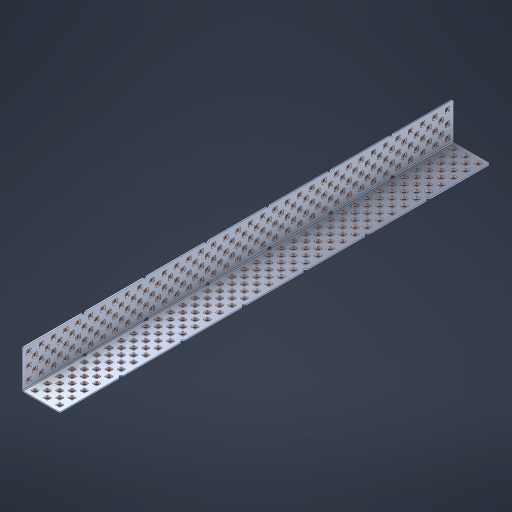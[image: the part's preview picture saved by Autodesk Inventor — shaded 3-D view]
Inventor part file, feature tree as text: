
AUTODESK INVENTOR PART (.ipt)
format: ipt  version: 2023 (Build 270158000, 158)  size: 3,399,680 bytes
history: native  units: in
note: dims shown in document units (in); Inventor stores cm internally (conversion verified against a paired STEP export)
features: other x352, extrude x344, sheet_metal_op x8, sketch x7, pattern_linear x3, mirror x1, chamfer x1
ambient origin geometry x8: Origin, YZ Plane, XZ Plane, XY Plane, X Axis, Y Axis, Z Axis, Center Point
bodies: Solid1 (feature_tree), Body (feature_tree)
feature tree (716):
  sheet_metal_op  "Flanges"
  sheet_metal_op  "Body Pattern"
  pattern_linear  "Center Double"  Spacing1=1.5in  [1 undecoded]
  pattern_linear  "Center Pattern"  Spacing1=0.1875in  [1 undecoded]
  other  "Arc Length"
  pattern_linear  "Notch Pattern"  Spacing1=0.0469in  [1 undecoded]
  other  "Diagonal Plane"
  mirror  "Everything Mirrored"
  chamfer  "End Chamfer"
  sketch  "Sketch1"  dims[d0=1.5in]
  other  "Plate1"
  sketch  "Sketch2"  dims[d1=17.5in]
  other  "Plate2"
  sheet_metal_op  "Bend1"
  sheet_metal_op  "Corner1"
  sketch  "Sketch8"  dims[d2=0.0469in]
  sketch  "Sketch9"  dims[d3=0.0469in]
  other  "Srf91"
  sheet_metal_op  "Body Pattern Sketch"
  other  "Srf92"
  sketch  "Sketch13"  dims[d4=0.0234in]
  sketch  "Sketch15"  dims[d5=0.0938in]
  sketch  "Sketch16"  dims[d6=0.0469in d7=1.5in d8=90.0deg d9=0.0312in d10=0.1875in d11=0.0469in d12=0.0469in d49=0.182in d50=0.02in d52=0.25in d53=0.0469in d54=0.0in d55=0.172in d56=1.0in d57=0.0in d85=0.1473in d86=0.1659in d89=0.0469in d90=0.0in d91=0.04in d92=0.0491in d95=2.5in d96=0.04in d97=0.25in d98=45.0deg d106=0.182in d107=0.02in d110=0.0469in d111=0.0in d112=0.172in d113=0.5in d114=0.0in d117=0.5in d126=0.0491in d127=0.1227in d128=0.08in d129=0.04in d130=2.5in d131=0.25in d132=13.7795in d134=0.5in d135=1.1811in d137=0.5in d140=0.5in d141=1.0in d142=0.3937in d144=0.5in d145=0.071in d146=0.7874in d148=0.5in]
  other  "Srf786"
  other  "Srf856"
  other  "Srf889"
  other  "Srf890"
  other  "Srf891"
  other  "Srf1275"
  other  "Srf1276"
  other  "Srf1278"
  other  "Srf1277"
  other  "Srf1285"
  other  "Srf1286"
  other  "Srf1287"
  other  "Srf1445"
  other  "Srf1446"
  other  "Srf1447"
  other  "Srf1448"
  other  "Srf1449"
  other  "Srf1537"
  other  "Srf1538"
  other  "Srf1539"
  other  "Srf1540"
  other  "Srf1541"
  other  "Srf1807"
  other  "Srf1808"
  other  "Srf1809"
  other  "Srf1810"
  other  "Srf1811"
  other  "Srf1812"
  other  "Srf1813"
  other  "Srf1814"
  other  "Srf1815"
  other  "Srf1816"
  other  "Srf1817"
  other  "Srf1818"
  other  "Srf1819"
  other  "Srf1820"
  other  "Srf1821"
  other  "Srf1822"
  other  "Srf1823"
  other  "Srf1824"
  other  "Srf1825"
  other  "Srf1826"
  other  "Srf1827"
  other  "Srf1828"
  other  "Srf1829"
  other  "Srf1830"
  other  "Srf1831"
  other  "Srf1959"
  other  "Srf1960"
  other  "Srf1961"
  other  "Srf1962"
  other  "Srf1963"
  other  "Srf1964"
  other  "Srf1965"
  other  "Srf1966"
  other  "Srf1967"
  other  "Srf1968"
  other  "Srf1969"
  other  "Srf1970"
  other  "Srf1971"
  other  "Srf1972"
  other  "Srf1973"
  other  "Srf1974"
  other  "Srf1975"
  other  "Srf1976"
  other  "Srf1977"
  other  "Srf1978"
  other  "Srf1979"
  other  "Srf1980"
  other  "Srf1981"
  other  "Srf1982"
  other  "Srf1983"
  other  "Srf2009"
  other  "Srf2010"
  other  "Srf2011"
  other  "Srf2012"
  other  "Srf2013"
  other  "Srf2014"
  other  "Srf2015"
  other  "Srf2016"
  other  "Srf2017"
  other  "Srf2018"
  other  "Srf2019"
  other  "Srf2020"
  other  "Srf2021"
  other  "Srf2022"
  other  "Srf2023"
  other  "Srf2024"
  other  "Srf2025"
  other  "Srf2026"
  other  "Srf2027"
  other  "Srf2028"
  other  "Srf2029"
  other  "Srf2030"
  other  "Srf2031"
  other  "Srf2032"
  other  "Srf2033"
  other  "Srf2034"
  other  "Srf2035"
  other  "Srf2036"
  other  "Srf2037"
  other  "Srf2038"
  other  "Srf2039"
  other  "Srf2040"
  other  "Srf2041"
  other  "Srf2042"
  other  "Srf2043"
  other  "Srf2044"
  other  "Srf2045"
  other  "Srf2046"
  other  "Srf2047"
  other  "Srf2048"
  other  "Srf2049"
  other  "Srf2050"
  other  "Srf2051"
  other  "Srf2052"
  other  "Srf2053"
  other  "Srf2054"
  other  "Srf2055"
  other  "Srf2056"
  other  "Srf2057"
  other  "Srf2058"
  other  "Srf2059"
  other  "Srf2060"
  other  "Srf2061"
  other  "Srf2062"
  other  "Srf2063"
  other  "Srf2064"
  other  "Srf2065"
  other  "Srf2066"
  other  "Srf2067"
  other  "Srf2068"
  other  "Srf2069"
  other  "Srf2070"
  other  "Srf2071"
  other  "Srf2072"
  other  "Srf2073"
  other  "Srf2074"
  other  "Srf2075"
  other  "Srf2076"
  other  "Srf2077"
  other  "Srf2078"
  other  "Srf2079"
  other  "Srf2080"
  other  "Srf2081"
  other  "Srf2082"
  other  "Srf2083"
  other  "Srf2084"
  other  "Srf2085"
  other  "Srf2086"
  other  "Srf2087"
  other  "Srf2088"
  other  "Srf2089"
  other  "Srf2090"
  other  "Srf2091"
  other  "Srf2092"
  other  "Srf2093"
  other  "Srf2094"
  other  "Srf2095"
  other  "Srf2096"
  other  "Srf2097"
  other  "Srf2098"
  other  "Srf2099"
  other  "Srf2100"
  other  "Srf2101"
  other  "Srf2102"
  other  "Srf2103"
  other  "Srf2104"
  other  "Srf2105"
  other  "Srf2106"
  other  "Srf2107"
  other  "Srf2108"
  other  "Srf2109"
  other  "Srf2110"
  other  "Srf2111"
  other  "Srf2112"
  other  "Srf2113"
  other  "Srf2114"
  other  "Srf2115"
  other  "Srf2116"
  other  "Srf2117"
  other  "Srf2118"
  other  "Srf2119"
  other  "Srf2120"
  other  "Srf2121"
  other  "Srf2122"
  other  "Srf2123"
  other  "Srf2124"
  other  "Srf2125"
  other  "Srf2126"
  other  "Srf2127"
  other  "Srf2128"
  other  "Srf2129"
  other  "Srf2130"
  other  "Srf2131"
  other  "Srf2132"
  other  "Srf2133"
  other  "Srf2134"
  other  "Srf2135"
  other  "Srf2136"
  other  "Srf2137"
  other  "Srf2138"
  other  "Srf2139"
  other  "Srf2140"
  other  "Srf2141"
  other  "Srf2142"
  other  "Srf2143"
  other  "Srf2144"
  other  "Srf2145"
  other  "Srf2146"
  other  "Srf2147"
  other  "Srf2148"
  other  "Srf2149"
  other  "Srf2150"
  other  "Srf2151"
  other  "Srf2152"
  other  "Srf2153"
  other  "Srf2154"
  other  "Srf2155"
  other  "Srf2156"
  other  "Srf2157"
  other  "Srf2158"
  other  "Srf2159"
  other  "Srf2160"
  other  "Srf2161"
  other  "Srf2162"
  other  "Srf2163"
  other  "Srf2164"
  other  "Srf2165"
  other  "Srf2166"
  other  "Srf2167"
  other  "Srf2168"
  other  "Srf2169"
  other  "Srf2170"
  other  "Srf2171"
  other  "Srf2172"
  other  "Srf2173"
  other  "Srf2174"
  other  "Srf2175"
  other  "Srf2176"
  other  "Srf2177"
  other  "Srf2178"
  other  "Srf2179"
  other  "Srf2180"
  other  "Srf2181"
  other  "Srf2182"
  other  "Srf2183"
  other  "Srf2184"
  other  "Srf2185"
  other  "Srf2186"
  other  "Srf2187"
  other  "Srf2188"
  other  "Srf2189"
  other  "Srf2190"
  other  "Srf2191"
  other  "Srf2192"
  other  "Srf2193"
  other  "Srf2194"
  other  "Srf2195"
  other  "Srf2196"
  other  "Srf2197"
  other  "Srf2198"
  other  "Srf2199"
  other  "Srf2200"
  other  "Srf2201"
  other  "Srf2202"
  other  "Srf2203"
  other  "Srf2204"
  other  "Srf2205"
  other  "Srf2206"
  other  "Srf2207"
  other  "Srf2208"
  other  "Srf2209"
  other  "Srf2210"
  other  "Srf2211"
  other  "Srf2212"
  other  "Srf2213"
  other  "Srf2214"
  other  "Srf2215"
  other  "Srf2216"
  other  "Srf2217"
  other  "Srf2218"
  other  "Srf2219"
  other  "Srf2220"
  other  "Srf2221"
  other  "Srf2222"
  other  "Srf2223"
  other  "Srf2224"
  other  "Srf2225"
  other  "Srf2226"
  other  "Srf2227"
  other  "Srf2228"
  other  "Srf2229"
  other  "Srf2230"
  other  "Srf2231"
  other  "Srf2232"
  other  "Srf2233"
  other  "Srf2234"
  other  "Srf2235"
  other  "Srf2236"
  other  "Srf2237"
  other  "Srf2238"
  other  "Srf2239"
  other  "Srf2240"
  other  "Srf2241"
  other  "Srf2242"
  other  "Srf2243"
  other  "Srf2244"
  other  "Srf2245"
  other  "Srf2246"
  other  "Srf2247"
  other  "Srf2248"
  other  "Srf2249"
  other  "Srf2250"
  other  "Srf2251"
  other  "Srf2252"
  other  "Srf2253"
  other  "Srf2254"
  other  "Srf2255"
  other  "Srf2256"
  other  "Srf2257"
  other  "Srf2258"
  other  "Srf2259"
  other  "Srf2260"
  other  "Srf2261"
  other  "Srf2262"
  other  "Srf2263"
  other  "Srf2264"
  other  "Srf2265"
  other  "Srf2266"
  other  "Srf2267"
  other  "Srf2268"
  other  "Srf2269"
  other  "Srf2270"
  other  "Srf2271"
  other  "Srf2272"
  other  "Srf2273"
  other  "Srf2274"
  other  "Srf2275"
  other  "Srf2276"
  other  "Srf2277"
  other  "Srf2278"
  other  "Srf2279"
  other  "Srf2280"
  sheet_metal_op  "Body Stamp"
  sheet_metal_op  "Body Circle"
  other  "Center Stamp"
  other  "Center Circle"
  sheet_metal_op  "Notch"
  extrude  "ExtrusionSrf92"  Depth=0.0469in
  extrude  "ExtrusionSrf856"  Depth=0.3937in
  extrude  "ExtrusionSrf889"  Depth=0.02in
  extrude  "ExtrusionSrf890"  Depth=0.25in
  extrude  "ExtrusionSrf891"  Depth=0.0469in
  extrude  "ExtrusionSrf1275"  TaperAngle=0.0deg  [1 undecoded]
  extrude  "ExtrusionSrf1276"  Depth=0.3937in
  extrude  "ExtrusionSrf1277"  Depth=0.3937in TaperAngle=0.0deg
  extrude  "ExtrusionSrf1345"  Depth=0.3937in
  extrude  "ExtrusionSrf1346"  Depth=0.3937in
  extrude  "ExtrusionSrf1347"  Depth=0.0469in
  extrude  "ExtrusionSrf1348"  Depth=0.3937in TaperAngle=0.0deg
  extrude  "ExtrusionSrf1445"  Depth=0.3937in
  extrude  "ExtrusionSrf1446"  Depth=0.25in TaperAngle=45.0deg
  extrude  "ExtrusionSrf1447"  Depth=0.3937in
  extrude  "ExtrusionSrf1448"  Depth=0.02in
  extrude  "ExtrusionSrf1449"  Depth=0.0469in
  extrude  "ExtrusionSrf1537"  TaperAngle=0.0deg  [1 undecoded]
  extrude  "ExtrusionSrf1538"  Depth=0.3937in
  extrude  "ExtrusionSrf1539"  Depth=0.3937in TaperAngle=0.0deg
  extrude  "ExtrusionSrf1540"  Depth=0.3937in
  extrude  "ExtrusionSrf1541"  Depth=0.3937in
  extrude  "ExtrusionSrf1807"  Depth=0.3937in
  extrude  "ExtrusionSrf1808"  Depth=0.3937in
  extrude  "ExtrusionSrf1809"  Depth=0.3937in
  extrude  "ExtrusionSrf1810"  Depth=0.3937in
  extrude  "ExtrusionSrf1811"  Depth=0.25in
  extrude  "ExtrusionSrf1812"  Depth=0.3937in
  extrude  "ExtrusionSrf1813"  Depth=0.3937in
  extrude  "ExtrusionSrf1814"  Depth=0.3937in
  extrude  "ExtrusionSrf1815"  Depth=0.3937in
  extrude  "ExtrusionSrf1816"  Depth=0.3937in
  extrude  "ExtrusionSrf1817"  Depth=0.3937in
  extrude  "ExtrusionSrf1818"  Depth=0.3937in
  extrude  "ExtrusionSrf1819"  [1 undecoded]
  extrude  "ExtrusionSrf1820"  [1 undecoded]
  extrude  "ExtrusionSrf1821"  [1 undecoded]
  extrude  "ExtrusionSrf1822"  [1 undecoded]
  extrude  "ExtrusionSrf1823"  [1 undecoded]
  extrude  "ExtrusionSrf1824"  [1 undecoded]
  extrude  "ExtrusionSrf1825"  [1 undecoded]
  extrude  "ExtrusionSrf1826"  [1 undecoded]
  extrude  "ExtrusionSrf1827"  [1 undecoded]
  extrude  "ExtrusionSrf1828"  [1 undecoded]
  extrude  "ExtrusionSrf1829"  [1 undecoded]
  extrude  "ExtrusionSrf1830"  [1 undecoded]
  extrude  "ExtrusionSrf1831"  [1 undecoded]
  extrude  "ExtrusionSrf1959"  [1 undecoded]
  extrude  "ExtrusionSrf1960"  [1 undecoded]
  extrude  "ExtrusionSrf1961"  [1 undecoded]
  extrude  "ExtrusionSrf1962"  [1 undecoded]
  extrude  "ExtrusionSrf1963"  [1 undecoded]
  extrude  "ExtrusionSrf1964"  [1 undecoded]
  extrude  "ExtrusionSrf1965"  [1 undecoded]
  extrude  "ExtrusionSrf1966"  [1 undecoded]
  extrude  "ExtrusionSrf1967"  [1 undecoded]
  extrude  "ExtrusionSrf1968"  [1 undecoded]
  extrude  "ExtrusionSrf1969"  [1 undecoded]
  extrude  "ExtrusionSrf1970"  [1 undecoded]
  extrude  "ExtrusionSrf1971"  [1 undecoded]
  extrude  "ExtrusionSrf1972"  [1 undecoded]
  extrude  "ExtrusionSrf1973"  [1 undecoded]
  extrude  "ExtrusionSrf1974"  [1 undecoded]
  extrude  "ExtrusionSrf1975"  [1 undecoded]
  extrude  "ExtrusionSrf1976"  [1 undecoded]
  extrude  "ExtrusionSrf1977"  [1 undecoded]
  extrude  "ExtrusionSrf1978"  [1 undecoded]
  extrude  "ExtrusionSrf1979"  [1 undecoded]
  extrude  "ExtrusionSrf1980"  [1 undecoded]
  extrude  "ExtrusionSrf1981"  [1 undecoded]
  extrude  "ExtrusionSrf1982"  [1 undecoded]
  extrude  "ExtrusionSrf1983"  [1 undecoded]
  extrude  "ExtrusionSrf2009"  [1 undecoded]
  extrude  "ExtrusionSrf2010"  [1 undecoded]
  extrude  "ExtrusionSrf2011"  [1 undecoded]
  extrude  "ExtrusionSrf2012"  [1 undecoded]
  extrude  "ExtrusionSrf2013"  [1 undecoded]
  extrude  "ExtrusionSrf2014"  [1 undecoded]
  extrude  "ExtrusionSrf2015"  [1 undecoded]
  extrude  "ExtrusionSrf2016"  [1 undecoded]
  extrude  "ExtrusionSrf2017"  [1 undecoded]
  extrude  "ExtrusionSrf2018"  [1 undecoded]
  extrude  "ExtrusionSrf2019"  [1 undecoded]
  extrude  "ExtrusionSrf2020"  [1 undecoded]
  extrude  "ExtrusionSrf2021"  [1 undecoded]
  extrude  "ExtrusionSrf2022"  [1 undecoded]
  extrude  "ExtrusionSrf2023"  [1 undecoded]
  extrude  "ExtrusionSrf2024"  [1 undecoded]
  extrude  "ExtrusionSrf2025"  [1 undecoded]
  extrude  "ExtrusionSrf2026"  [1 undecoded]
  extrude  "ExtrusionSrf2027"  [1 undecoded]
  extrude  "ExtrusionSrf2028"  [1 undecoded]
  extrude  "ExtrusionSrf2029"  [1 undecoded]
  extrude  "ExtrusionSrf2030"  [1 undecoded]
  extrude  "ExtrusionSrf2031"  [1 undecoded]
  extrude  "ExtrusionSrf2032"  [1 undecoded]
  extrude  "ExtrusionSrf2033"  [1 undecoded]
  extrude  "ExtrusionSrf2034"  [1 undecoded]
  extrude  "ExtrusionSrf2035"  [1 undecoded]
  extrude  "ExtrusionSrf2036"  [1 undecoded]
  extrude  "ExtrusionSrf2037"  [1 undecoded]
  extrude  "ExtrusionSrf2038"  [1 undecoded]
  extrude  "ExtrusionSrf2039"  [1 undecoded]
  extrude  "ExtrusionSrf2040"  [1 undecoded]
  extrude  "ExtrusionSrf2041"  [1 undecoded]
  extrude  "ExtrusionSrf2042"  [1 undecoded]
  extrude  "ExtrusionSrf2043"  [1 undecoded]
  extrude  "ExtrusionSrf2044"  [1 undecoded]
  extrude  "ExtrusionSrf2045"  [1 undecoded]
  extrude  "ExtrusionSrf2046"  [1 undecoded]
  extrude  "ExtrusionSrf2047"  [1 undecoded]
  extrude  "ExtrusionSrf2048"  [1 undecoded]
  extrude  "ExtrusionSrf2049"  [1 undecoded]
  extrude  "ExtrusionSrf2050"  [1 undecoded]
  extrude  "ExtrusionSrf2051"  [1 undecoded]
  extrude  "ExtrusionSrf2052"  [1 undecoded]
  extrude  "ExtrusionSrf2053"  [1 undecoded]
  extrude  "ExtrusionSrf2054"  [1 undecoded]
  extrude  "ExtrusionSrf2055"  [1 undecoded]
  extrude  "ExtrusionSrf2056"  [1 undecoded]
  extrude  "ExtrusionSrf2057"  [1 undecoded]
  extrude  "ExtrusionSrf2058"  [1 undecoded]
  extrude  "ExtrusionSrf2059"  [1 undecoded]
  extrude  "ExtrusionSrf2060"  [1 undecoded]
  extrude  "ExtrusionSrf2061"  [1 undecoded]
  extrude  "ExtrusionSrf2062"  [1 undecoded]
  extrude  "ExtrusionSrf2063"  [1 undecoded]
  extrude  "ExtrusionSrf2064"  [1 undecoded]
  extrude  "ExtrusionSrf2065"  [1 undecoded]
  extrude  "ExtrusionSrf2066"  [1 undecoded]
  extrude  "ExtrusionSrf2067"  [1 undecoded]
  extrude  "ExtrusionSrf2068"  [1 undecoded]
  extrude  "ExtrusionSrf2069"  [1 undecoded]
  extrude  "ExtrusionSrf2070"  [1 undecoded]
  extrude  "ExtrusionSrf2071"  [1 undecoded]
  extrude  "ExtrusionSrf2072"  [1 undecoded]
  extrude  "ExtrusionSrf2073"  [1 undecoded]
  extrude  "ExtrusionSrf2074"  [1 undecoded]
  extrude  "ExtrusionSrf2075"  [1 undecoded]
  extrude  "ExtrusionSrf2076"  [1 undecoded]
  extrude  "ExtrusionSrf2077"  [1 undecoded]
  extrude  "ExtrusionSrf2078"  [1 undecoded]
  extrude  "ExtrusionSrf2079"  [1 undecoded]
  extrude  "ExtrusionSrf2080"  [1 undecoded]
  extrude  "ExtrusionSrf2081"  [1 undecoded]
  extrude  "ExtrusionSrf2082"  [1 undecoded]
  extrude  "ExtrusionSrf2083"  [1 undecoded]
  extrude  "ExtrusionSrf2084"  [1 undecoded]
  extrude  "ExtrusionSrf2085"  [1 undecoded]
  extrude  "ExtrusionSrf2086"  [1 undecoded]
  extrude  "ExtrusionSrf2087"  [1 undecoded]
  extrude  "ExtrusionSrf2088"  [1 undecoded]
  extrude  "ExtrusionSrf2089"  [1 undecoded]
  extrude  "ExtrusionSrf2090"  [1 undecoded]
  extrude  "ExtrusionSrf2091"  [1 undecoded]
  extrude  "ExtrusionSrf2092"  [1 undecoded]
  extrude  "ExtrusionSrf2093"  [1 undecoded]
  extrude  "ExtrusionSrf2094"  [1 undecoded]
  extrude  "ExtrusionSrf2095"  [1 undecoded]
  extrude  "ExtrusionSrf2096"  [1 undecoded]
  extrude  "ExtrusionSrf2097"  [1 undecoded]
  extrude  "ExtrusionSrf2098"  [1 undecoded]
  extrude  "ExtrusionSrf2099"  [1 undecoded]
  extrude  "ExtrusionSrf2100"  [1 undecoded]
  extrude  "ExtrusionSrf2101"  [1 undecoded]
  extrude  "ExtrusionSrf2102"  [1 undecoded]
  extrude  "ExtrusionSrf2103"  [1 undecoded]
  extrude  "ExtrusionSrf2104"  [1 undecoded]
  extrude  "ExtrusionSrf2105"  [1 undecoded]
  extrude  "ExtrusionSrf2106"  [1 undecoded]
  extrude  "ExtrusionSrf2107"  [1 undecoded]
  extrude  "ExtrusionSrf2108"  [1 undecoded]
  extrude  "ExtrusionSrf2109"  [1 undecoded]
  extrude  "ExtrusionSrf2110"  [1 undecoded]
  extrude  "ExtrusionSrf2111"  [1 undecoded]
  extrude  "ExtrusionSrf2112"  [1 undecoded]
  extrude  "ExtrusionSrf2113"  [1 undecoded]
  extrude  "ExtrusionSrf2114"  [1 undecoded]
  extrude  "ExtrusionSrf2115"  [1 undecoded]
  extrude  "ExtrusionSrf2116"  [1 undecoded]
  extrude  "ExtrusionSrf2117"  [1 undecoded]
  extrude  "ExtrusionSrf2118"  [1 undecoded]
  extrude  "ExtrusionSrf2119"  [1 undecoded]
  extrude  "ExtrusionSrf2120"  [1 undecoded]
  extrude  "ExtrusionSrf2121"  [1 undecoded]
  extrude  "ExtrusionSrf2122"  [1 undecoded]
  extrude  "ExtrusionSrf2123"  [1 undecoded]
  extrude  "ExtrusionSrf2124"  [1 undecoded]
  extrude  "ExtrusionSrf2125"  [1 undecoded]
  extrude  "ExtrusionSrf2126"  [1 undecoded]
  extrude  "ExtrusionSrf2127"  [1 undecoded]
  extrude  "ExtrusionSrf2128"  [1 undecoded]
  extrude  "ExtrusionSrf2129"  [1 undecoded]
  extrude  "ExtrusionSrf2130"  [1 undecoded]
  extrude  "ExtrusionSrf2131"  [1 undecoded]
  extrude  "ExtrusionSrf2132"  [1 undecoded]
  extrude  "ExtrusionSrf2133"  [1 undecoded]
  extrude  "ExtrusionSrf2134"  [1 undecoded]
  extrude  "ExtrusionSrf2135"  [1 undecoded]
  extrude  "ExtrusionSrf2136"  [1 undecoded]
  extrude  "ExtrusionSrf2137"  [1 undecoded]
  extrude  "ExtrusionSrf2138"  [1 undecoded]
  extrude  "ExtrusionSrf2139"  [1 undecoded]
  extrude  "ExtrusionSrf2140"  [1 undecoded]
  extrude  "ExtrusionSrf2141"  [1 undecoded]
  extrude  "ExtrusionSrf2142"  [1 undecoded]
  extrude  "ExtrusionSrf2143"  [1 undecoded]
  extrude  "ExtrusionSrf2144"  [1 undecoded]
  extrude  "ExtrusionSrf2145"  [1 undecoded]
  extrude  "ExtrusionSrf2146"  [1 undecoded]
  extrude  "ExtrusionSrf2147"  [1 undecoded]
  extrude  "ExtrusionSrf2148"  [1 undecoded]
  extrude  "ExtrusionSrf2149"  [1 undecoded]
  extrude  "ExtrusionSrf2150"  [1 undecoded]
  extrude  "ExtrusionSrf2151"  [1 undecoded]
  extrude  "ExtrusionSrf2152"  [1 undecoded]
  extrude  "ExtrusionSrf2153"  [1 undecoded]
  extrude  "ExtrusionSrf2154"  [1 undecoded]
  extrude  "ExtrusionSrf2155"  [1 undecoded]
  extrude  "ExtrusionSrf2156"  [1 undecoded]
  extrude  "ExtrusionSrf2157"  [1 undecoded]
  extrude  "ExtrusionSrf2158"  [1 undecoded]
  extrude  "ExtrusionSrf2159"  [1 undecoded]
  extrude  "ExtrusionSrf2160"  [1 undecoded]
  extrude  "ExtrusionSrf2161"  [1 undecoded]
  extrude  "ExtrusionSrf2162"  [1 undecoded]
  extrude  "ExtrusionSrf2163"  [1 undecoded]
  extrude  "ExtrusionSrf2164"  [1 undecoded]
  extrude  "ExtrusionSrf2165"  [1 undecoded]
  extrude  "ExtrusionSrf2166"  [1 undecoded]
  extrude  "ExtrusionSrf2167"  [1 undecoded]
  extrude  "ExtrusionSrf2168"  [1 undecoded]
  extrude  "ExtrusionSrf2169"  [1 undecoded]
  extrude  "ExtrusionSrf2170"  [1 undecoded]
  extrude  "ExtrusionSrf2171"  [1 undecoded]
  extrude  "ExtrusionSrf2172"  [1 undecoded]
  extrude  "ExtrusionSrf2173"  [1 undecoded]
  extrude  "ExtrusionSrf2174"  [1 undecoded]
  extrude  "ExtrusionSrf2175"  [1 undecoded]
  extrude  "ExtrusionSrf2176"  [1 undecoded]
  extrude  "ExtrusionSrf2177"  [1 undecoded]
  extrude  "ExtrusionSrf2178"  [1 undecoded]
  extrude  "ExtrusionSrf2179"  [1 undecoded]
  extrude  "ExtrusionSrf2180"  [1 undecoded]
  extrude  "ExtrusionSrf2181"  [1 undecoded]
  extrude  "ExtrusionSrf2182"  [1 undecoded]
  extrude  "ExtrusionSrf2183"  [1 undecoded]
  extrude  "ExtrusionSrf2184"  [1 undecoded]
  extrude  "ExtrusionSrf2185"  [1 undecoded]
  extrude  "ExtrusionSrf2186"  [1 undecoded]
  extrude  "ExtrusionSrf2187"  [1 undecoded]
  extrude  "ExtrusionSrf2188"  [1 undecoded]
  extrude  "ExtrusionSrf2189"  [1 undecoded]
  extrude  "ExtrusionSrf2190"  [1 undecoded]
  extrude  "ExtrusionSrf2191"  [1 undecoded]
  extrude  "ExtrusionSrf2192"  [1 undecoded]
  extrude  "ExtrusionSrf2193"  [1 undecoded]
  extrude  "ExtrusionSrf2194"  [1 undecoded]
  extrude  "ExtrusionSrf2195"  [1 undecoded]
  extrude  "ExtrusionSrf2196"  [1 undecoded]
  extrude  "ExtrusionSrf2197"  [1 undecoded]
  extrude  "ExtrusionSrf2198"  [1 undecoded]
  extrude  "ExtrusionSrf2199"  [1 undecoded]
  extrude  "ExtrusionSrf2200"  [1 undecoded]
  extrude  "ExtrusionSrf2201"  [1 undecoded]
  extrude  "ExtrusionSrf2202"  [1 undecoded]
  extrude  "ExtrusionSrf2203"  [1 undecoded]
  extrude  "ExtrusionSrf2204"  [1 undecoded]
  extrude  "ExtrusionSrf2205"  [1 undecoded]
  extrude  "ExtrusionSrf2206"  [1 undecoded]
  extrude  "ExtrusionSrf2207"  [1 undecoded]
  extrude  "ExtrusionSrf2208"  [1 undecoded]
  extrude  "ExtrusionSrf2209"  [1 undecoded]
  extrude  "ExtrusionSrf2210"  [1 undecoded]
  extrude  "ExtrusionSrf2211"  [1 undecoded]
  extrude  "ExtrusionSrf2212"  [1 undecoded]
  extrude  "ExtrusionSrf2213"  [1 undecoded]
  extrude  "ExtrusionSrf2214"  [1 undecoded]
  extrude  "ExtrusionSrf2215"  [1 undecoded]
  extrude  "ExtrusionSrf2216"  [1 undecoded]
  extrude  "ExtrusionSrf2217"  [1 undecoded]
  extrude  "ExtrusionSrf2218"  [1 undecoded]
  extrude  "ExtrusionSrf2219"  [1 undecoded]
  extrude  "ExtrusionSrf2220"  [1 undecoded]
  extrude  "ExtrusionSrf2221"  [1 undecoded]
  extrude  "ExtrusionSrf2222"  [1 undecoded]
  extrude  "ExtrusionSrf2223"  [1 undecoded]
  extrude  "ExtrusionSrf2224"  [1 undecoded]
  extrude  "ExtrusionSrf2225"  [1 undecoded]
  extrude  "ExtrusionSrf2226"  [1 undecoded]
  extrude  "ExtrusionSrf2227"  [1 undecoded]
  extrude  "ExtrusionSrf2228"  [1 undecoded]
  extrude  "ExtrusionSrf2229"  [1 undecoded]
  extrude  "ExtrusionSrf2230"  [1 undecoded]
  extrude  "ExtrusionSrf2231"  [1 undecoded]
  extrude  "ExtrusionSrf2232"  [1 undecoded]
  extrude  "ExtrusionSrf2233"  [1 undecoded]
  extrude  "ExtrusionSrf2234"  [1 undecoded]
  extrude  "ExtrusionSrf2235"  [1 undecoded]
  extrude  "ExtrusionSrf2236"  [1 undecoded]
  extrude  "ExtrusionSrf2237"  [1 undecoded]
  extrude  "ExtrusionSrf2238"  [1 undecoded]
  extrude  "ExtrusionSrf2239"  [1 undecoded]
  extrude  "ExtrusionSrf2240"  [1 undecoded]
  extrude  "ExtrusionSrf2241"  [1 undecoded]
  extrude  "ExtrusionSrf2242"  [1 undecoded]
  extrude  "ExtrusionSrf2243"  [1 undecoded]
  extrude  "ExtrusionSrf2244"  [1 undecoded]
  extrude  "ExtrusionSrf2245"  [1 undecoded]
  extrude  "ExtrusionSrf2246"  [1 undecoded]
  extrude  "ExtrusionSrf2247"  [1 undecoded]
  extrude  "ExtrusionSrf2248"  [1 undecoded]
  extrude  "ExtrusionSrf2249"  [1 undecoded]
  extrude  "ExtrusionSrf2250"  [1 undecoded]
  extrude  "ExtrusionSrf2251"  [1 undecoded]
  extrude  "ExtrusionSrf2252"  [1 undecoded]
  extrude  "ExtrusionSrf2253"  [1 undecoded]
  extrude  "ExtrusionSrf2254"  [1 undecoded]
  extrude  "ExtrusionSrf2255"  [1 undecoded]
  extrude  "ExtrusionSrf2256"  [1 undecoded]
  extrude  "ExtrusionSrf2257"  [1 undecoded]
  extrude  "ExtrusionSrf2258"  [1 undecoded]
  extrude  "ExtrusionSrf2259"  [1 undecoded]
  extrude  "ExtrusionSrf2260"  [1 undecoded]
  extrude  "ExtrusionSrf2261"  [1 undecoded]
  extrude  "ExtrusionSrf2262"  [1 undecoded]
  extrude  "ExtrusionSrf2263"  [1 undecoded]
  extrude  "ExtrusionSrf2264"  [1 undecoded]
  extrude  "ExtrusionSrf2265"  [1 undecoded]
  extrude  "ExtrusionSrf2266"  [1 undecoded]
  extrude  "ExtrusionSrf2267"  [1 undecoded]
  extrude  "ExtrusionSrf2268"  [1 undecoded]
  extrude  "ExtrusionSrf2269"  [1 undecoded]
  extrude  "ExtrusionSrf2270"  [1 undecoded]
  extrude  "ExtrusionSrf2271"  [1 undecoded]
  extrude  "ExtrusionSrf2272"  [1 undecoded]
  extrude  "ExtrusionSrf2273"  [1 undecoded]
  extrude  "ExtrusionSrf2274"  [1 undecoded]
  extrude  "ExtrusionSrf2275"  [1 undecoded]
  extrude  "ExtrusionSrf2276"  [1 undecoded]
  extrude  "ExtrusionSrf2277"  [1 undecoded]
  extrude  "ExtrusionSrf2278"  [1 undecoded]
  extrude  "ExtrusionSrf2279"  [1 undecoded]
  extrude  "ExtrusionSrf2280"  [1 undecoded]
note: 315 required parameter values undecoded (feature->parameter linkage not recoverable at this tier; creation-order binding heuristic only, values carry confidence <= 0.55)
